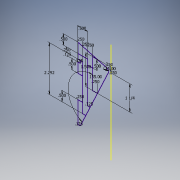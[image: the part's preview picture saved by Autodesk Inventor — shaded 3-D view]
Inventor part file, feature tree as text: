
AUTODESK INVENTOR PART (.ipt)
format: ipt  version: 2017 (Build 210142000, 142)  size: 116,224 bytes
history: native  units: in
note: dims shown in document units (in); Inventor stores cm internally (conversion verified against a paired STEP export)
features: sketch x1
ambient origin geometry x8: Origin, YZ Plane, XZ Plane, XY Plane, X Axis, Y Axis, Z Axis, Center Point
feature tree (1):
  sketch  "Sketch1"  dims[d0=0.25in d1=0.1718in d2=15.0deg d4=0.25in d5=1.5in d6=1.25in d7=0.25in d11=0.25in d13=0.5in d15=0.25in d16=0.25in d18=0.125in d19=0.5in d20=0.125in d21=0.25in d22=0.125in d23=0.125in d24=0.25in d25=0.5in d26=2.292in d27=0.5in d29=0.5in]
